# Revit family: Shape190807
name_source: partatom
category: Furniture
units: mm (PartAtom-declared; Revit-internal decimal feet)

## family parameters
Always vertical = Yes
Cut with Voids When Loaded = No
OmniClass Number = 23.40.20.00
OmniClass Title = General Furniture and Specialties
Room Calculation Point = No
Shared = No
Work Plane-Based = No

## types (30) — shared parameters
Body material = Chip board moisture resistant E1 and FSC certified
Svulsthöjd = 752 mm

## per-type parameters (varying)
| type | Article number | Depth | Finish | Fronts material | GTIN | Manufacturer | Model | URL | Width |
| Shape 600 white matt | 1390200 | 439 mm  [stored 1.44029 ft] | NCS S 0300-N 20% gloss | MDF moisture resistand E1 and FSC resistant. | 7330027109442 | Hafa Bathroom Group AB | Shape | www.hafa.se | 600 mm  [stored 1.9685 ft] |
| Shape 800 white matt | 1390205 | 439 mm  [stored 1.44029 ft] | NCS S 0300-N 20% gloss | MDF moisture resistand E1 and FSC resistant. | 7330027109497 |  |  |  | 800 mm  [stored 2.62467 ft] |
| Shape 900 white matt | 1390210 | 439 mm  [stored 1.44029 ft] | NCS S 0300-N 20% gloss | MDF moisture resistand E1 and FSC resistant. | 7330027109541 |  |  |  | 900 mm  [stored 2.95276 ft] |
| Shape 1000 white matt | 1390215 | 439 mm  [stored 1.44029 ft] | NCS S 0300-N 20% gloss | MDF moisture resistand E1 and FSC resistant. | 7330027109596 |  |  |  | 1000 mm  [stored 3.28084 ft] |
| Shape compact 600 white matt | 1390224 | 369 mm | NCS S 0300-N 20% gloss | MDF moisture resistand E1 and FSC resistant. | 7330027109688 |  |  |  | 600 mm  [stored 1.9685 ft] |
| Shape compact 800 white matt | 1390233 | 369 mm | NCS S 0300-N 20% gloss | MDF moisture resistand E1 and FSC resistant. | 7330027109770 |  |  |  | 800 mm  [stored 2.62467 ft] |
| Shape 600 grey matt | 1390203 | 439 mm  [stored 1.44029 ft] | NCS S 4500-N 10% gloss | MDF moisture resistand E1 and FSC resistant. | 7330027109473 |  |  |  | 600 mm  [stored 1.9685 ft] |
| Shape 1000 grey matt | 1390218 | 439 mm  [stored 1.44029 ft] | NCS S 4500-N 10% gloss | MDF moisture resistand E1 and FSC resistant. | 7330027109626 |  |  |  | 1000 mm  [stored 3.28084 ft] |
| Shape 800 grey matt | 1390208 | 439 mm  [stored 1.44029 ft] | NCS S 4500-N 10% gloss | MDF moisture resistand E1 and FSC resistant. | 7330027109527 |  |  |  | 800 mm  [stored 2.62467 ft] |
| Shape 900 grey matt | 1390213 | 439 mm  [stored 1.44029 ft] | NCS S 4500-N 10% gloss | MDF moisture resistand E1 and FSC resistant. | 7330027109572 |  |  |  | 900 mm  [stored 2.95276 ft] |
| Shape compact 600 grey matt | 1390227 | 369 mm | NCS S 4500-N 10% gloss | MDF moisture resistand E1 and FSC resistant. | 7330027109718 |  |  |  | 600 mm  [stored 1.9685 ft] |
| Shape compact 800 grey matt | 1390236 | 369 mm | NCS S 4500-N 10% gloss | MDF moisture resistand E1 and FSC resistant. | 7330027109800 |  |  |  | 800 mm  [stored 2.62467 ft] |
| Shape 600 Ash foil | 1390204 | 439 mm  [stored 1.44029 ft] | Ash foil | MDF moisture resistand E1 and FSC resistant. | 7330027109480 |  |  |  | 600 mm  [stored 1.9685 ft] |
| Shape 1000 anthracite matt | 1390216 | 439 mm  [stored 1.44029 ft] | NCS S 8000-N 10% gloss | MDF moisture resistand E1 and FSC resistant. | 7330027109602 |  |  |  | 1000 mm  [stored 3.28084 ft] |
| Shape 1000 ash foil | 1390219 | 439 mm  [stored 1.44029 ft] | Ash foil | MDF moisture resistand E1 and FSC resistant. | 7330027109633 |  |  |  | 1000 mm  [stored 3.28084 ft] |
| Shape 1000 white high gloss | 1390217 | 439 mm  [stored 1.44029 ft] | NCS S 0300-N 90% gloss | MDF moisture resistand E1 and FSC resistant. | 7330027109619 |  |  |  | 1000 mm  [stored 3.28084 ft] |
| Shape 600 white high gloss | 1390202 | 439 mm  [stored 1.44029 ft] | NCS S 0300-N 90% gloss | MDF moisture resistand E1 and FSC resistant. | 7330027109466 | Hafa Bathroom Group AB | Shape | www.hafa.se | 600 mm  [stored 1.9685 ft] |
| Shape 600 anthracite matt | 1390201 | 439 mm  [stored 1.44029 ft] | NCS S 8000-N 10% gloss | MDF moisture resistand E1 and FSC resistant. | 7330027109459 | Hafa Bathroom Group AB | Shape | www.hafa.se | 600 mm  [stored 1.9685 ft] |
| Shape 800 ash foil | 1390209 | 439 mm  [stored 1.44029 ft] | Ash foil | MDF moisture resistand E1 and FSC resistant. | 7330027109534 |  |  |  | 800 mm  [stored 2.62467 ft] |
| Shape 800 white high gloss | 1390207 | 439 mm  [stored 1.44029 ft] | NCS S 0300-N 90% gloss | MDF moisture resistand E1 and FSC resistant. | 7330027109510 |  |  |  | 800 mm  [stored 2.62467 ft] |
| Shape 800 anthractie matt | 1390206 | 439 mm  [stored 1.44029 ft] | NCS S 8000-N 10% gloss | MDF moisture resistand E1 and FSC resistant. | 7330027109503 |  |  |  | 800 mm  [stored 2.62467 ft] |
| Shape 900 white high gloss | 1390212 | 439 mm  [stored 1.44029 ft] | NCS S 0300-N 90% gloss | MDF moisture resistand E1 and FSC resistant. | 7330027109565 |  |  |  | 900 mm  [stored 2.95276 ft] |
| Shape 900 ash foil | 1390214 | 439 mm  [stored 1.44029 ft] | Ash foil | MDF moisture resistand E1 and FSC resistant. | 7330027109589 |  |  |  | 900 mm  [stored 2.95276 ft] |
| Shape 900 anthracite matt | 1390211 | 439 mm  [stored 1.44029 ft] | NCS S 8000-N 10% gloss | MDF moisture resistand E1 and FSC resistant. | 7330027109558 |  |  |  | 900 mm  [stored 2.95276 ft] |
| Shape compact 600 white high gloss | 1390226 | 369 mm | NCS S 0300-N 90% gloss | MDF moisture resistand E1 and FSC resistant. | 7330027109701 |  |  |  | 600 mm  [stored 1.9685 ft] |
| Shape compact 600 anthracite matt | 1390225 | 369 mm | NCS S 8000-N 10% gloss | MDF moisture resistand E1 and FSC resistant. | 7330027109695 |  |  |  | 600 mm  [stored 1.9685 ft] |
| Shape compact 600 ash foil | 1390228 | 369 mm | Ash foil |  | 7330027109725 |  |  |  | 600 mm  [stored 1.9685 ft] |
| Shape compact 800 white high gloss | 1390235 | 369 mm | NCS S 0300-N 90% gloss | MDF moisture resistand E1 and FSC resistant. | 7330027109794 |  |  |  | 800 mm  [stored 2.62467 ft] |
| Shape compact 800 ash foil | 1390237 | 369 mm | Ash foil | MDF moisture resistand E1 and FSC resistant. | 7330027109817 |  |  |  | 800 mm  [stored 2.62467 ft] |
| Shape compact 800 anthracite matt | 1390234 | 369 mm | NCS S 8000-N 10% gloss | MDF moisture resistand E1 and FSC resistant. | 7330027109787 |  |  |  | 800 mm  [stored 2.62467 ft] |

note: [stored X ft] marks values corroborated as IEEE doubles in the binary element streams (Revit-internal decimal feet)

## geometry (parser evidence)
native form markers: Sweep x6
no freeform markers — native parametric forms only
